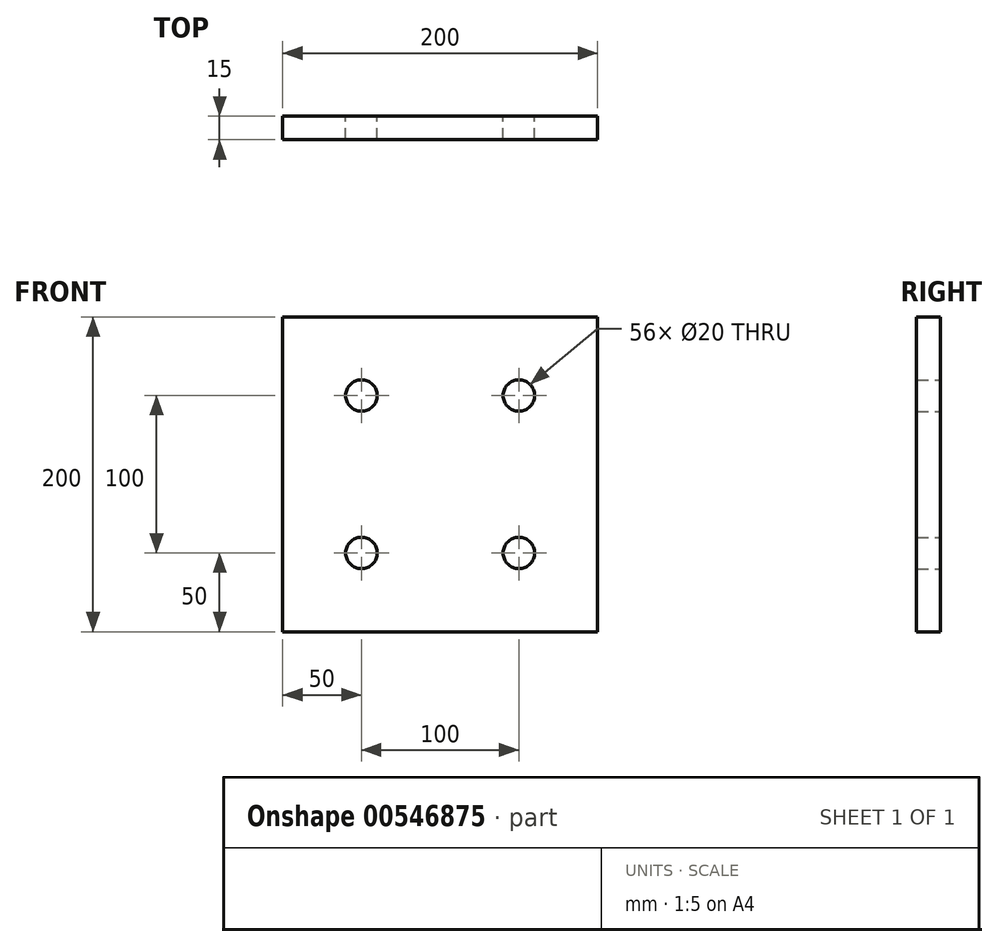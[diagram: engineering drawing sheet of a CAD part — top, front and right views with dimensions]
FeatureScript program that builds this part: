
annotation { "Feature Type Name" : "Feature", "Feature Type Description" : "" }
export const myFeature = defineFeature(function(context is Context, id is Id, definition is map)
    precondition{}
    {
        {
            var Q0;
            Q0=qCreatedBy(makeId("Front.planeOp"),FACE);
            var sketch = newSketch(context, id + "F0", { "sketchPlane" : qUnion([Q0])});
            skLineSegment(sketch, "E0.bottom", {"start": v(100, 100) * mm, "end": v(-100, 100) * mm});
            skLineSegment(sketch, "E0.top", {"start": v(100, -100) * mm, "end": v(-100, -100) * mm});
            skLineSegment(sketch, "E0.left", {"start": v(100, 100) * mm, "end": v(100, -100) * mm});
            skLineSegment(sketch, "E0.right", {"start": v(-100, 100) * mm, "end": v(-100, -100) * mm});
            skPoint(sketch, "E0.middle", {"position": v(0, 0) * mm});
            skCircle(sketch, "E1", {"center": v(-50, -50) * mm, "radius": 10 * mm});
            skCircle(sketch, "E2", {"center": v(50, -50) * mm, "radius": 10 * mm});
            skCircle(sketch, "E3", {"center": v(-50, 50) * mm, "radius": 10 * mm});
            skCircle(sketch, "E4", {"center": v(50, 50) * mm, "radius": 10 * mm});
            skSolve(sketch);
        }
        {
            var Q0;
            Q0=makeQuery(id+"F0.imprint","IMPRINT",FACE,{"disambiguationData":[TD([[makeQuery(id+"F0.imprint","IMPRINT",EDGE,{"derivedFrom":sQuery(id+"F0.wireOp",EDGE,"E0.bottom")}),1.0]])]});
            extrude(context, id + "F1", {"entities" : qUnion([Q0]), "endBound" : BoundingType.SYMMETRIC, "depth" : 15 * mm, "offsetDistance" : 25 * mm});
        }
    });
